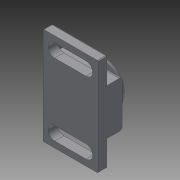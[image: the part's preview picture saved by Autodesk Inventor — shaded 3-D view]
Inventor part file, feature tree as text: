
AUTODESK INVENTOR PART (.ipt)
format: ipt  version: 2015 SP1 (Build 190203100, 203)  size: 169,472 bytes
history: native  units: mm
features: sketch x5, extrude x4, fillet x2, plane x1, revolve x1, projected_geometry x1
ambient origin geometry x8: Origin, YZ Plane, XZ Plane, XY Plane, X Axis, Y Axis, Z Axis, Center Point
bodies: Solid1 (feature_tree)
feature tree (14):
  extrude  "Extrusion1"  Depth=53.0mm
  extrude  "Extrusion2"  Depth=14.0mm
  extrude  "Extrusion3"  Depth=8.0mm TaperAngle=0.0deg
  plane  "Work Plane1"
  revolve  "Revolution1"  [1 undecoded]
  extrude  "Extrusion4"  Depth=1.5mm TaperAngle=0.0deg
  fillet  "Fillet1"  Radius=0.5mm
  fillet  "Fillet2"  Radius=1.5mm
  sketch  "Sketch1"  dims[d0=30.0mm d1=53.0mm]
  sketch  "Sketch2"  dims[d2=5.0mm d3=0.0mm d4=14.0mm]
  sketch  "Sketch3"  dims[d5=14.0mm d6=8.0mm d7=0.0mm]
  sketch  "Sketch4"  dims[d8=15.0mm d9=3.0mm d10=0.0mm]
  projected_geometry  "Projected Loop1"
  sketch  "Sketch5"  dims[d12=90.0deg d13=32.0mm d14=0.0mm d15=0.5mm d16=1.5mm]
note: 1 required parameter value undecoded (feature->parameter linkage not recoverable at this tier; creation-order binding heuristic only, values carry confidence <= 0.55)
